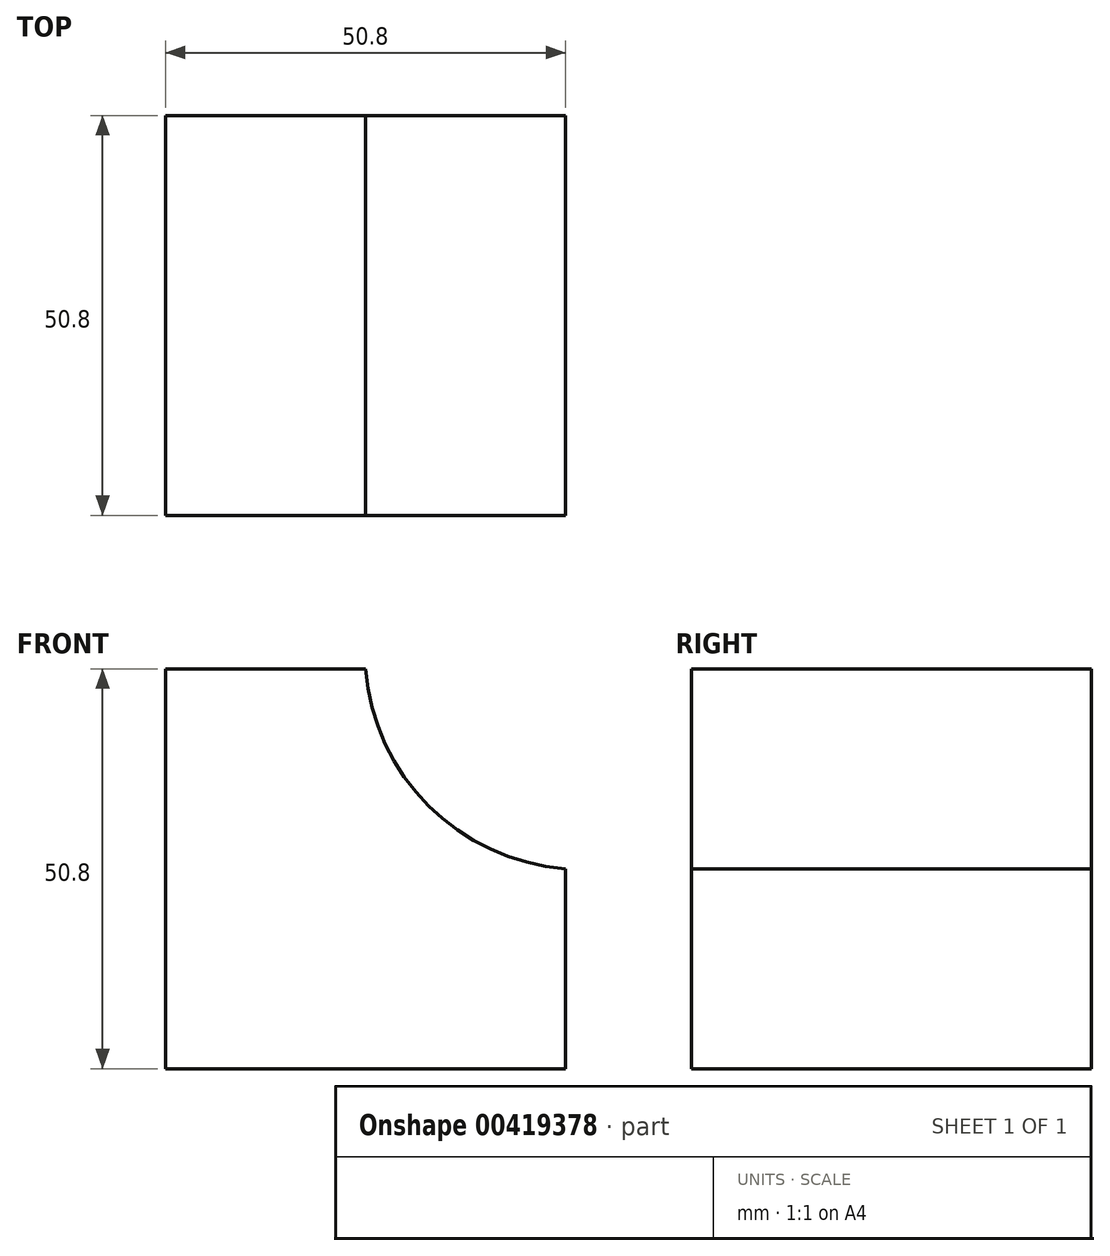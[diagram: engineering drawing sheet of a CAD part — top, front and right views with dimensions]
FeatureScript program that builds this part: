
annotation { "Feature Type Name" : "Feature", "Feature Type Description" : "" }
export const myFeature = defineFeature(function(context is Context, id is Id, definition is map)
    precondition{}
    {
        {
            var Q0;
            Q0=qCreatedBy(makeId("Front.planeOp"),FACE);
            var sketch = newSketch(context, id + "F0", { "sketchPlane" : qUnion([Q0])});
            skLineSegment(sketch, "E0", {"start": v(0, 0) * mm, "end": v(0, 50.8) * mm});
            skLineSegment(sketch, "E1", {"start": v(0, 0) * mm, "end": v(50.8, 0) * mm});
            skLineSegment(sketch, "E2", {"start": v(0, 50.8) * mm, "end": v(25.4, 50.8) * mm});
            skLineSegment(sketch, "E3", {"start": v(50.8, 0) * mm, "end": v(50.8, 25.4) * mm});
            skArc(sketch, "E4", {"start": v(25.4, 50.8) * mm, "mid": v(33.4, 33.4) * mm, "end": v(50.8, 25.4) * mm});
            skSolve(sketch);
        }
        {
            var Q0;
            Q0 = qSketchRegion(id + "F0", true);
            extrude(context, id + "F1", {"entities" : qUnion([Q0]), "depth" : 50.8 * mm});
        }
    });
